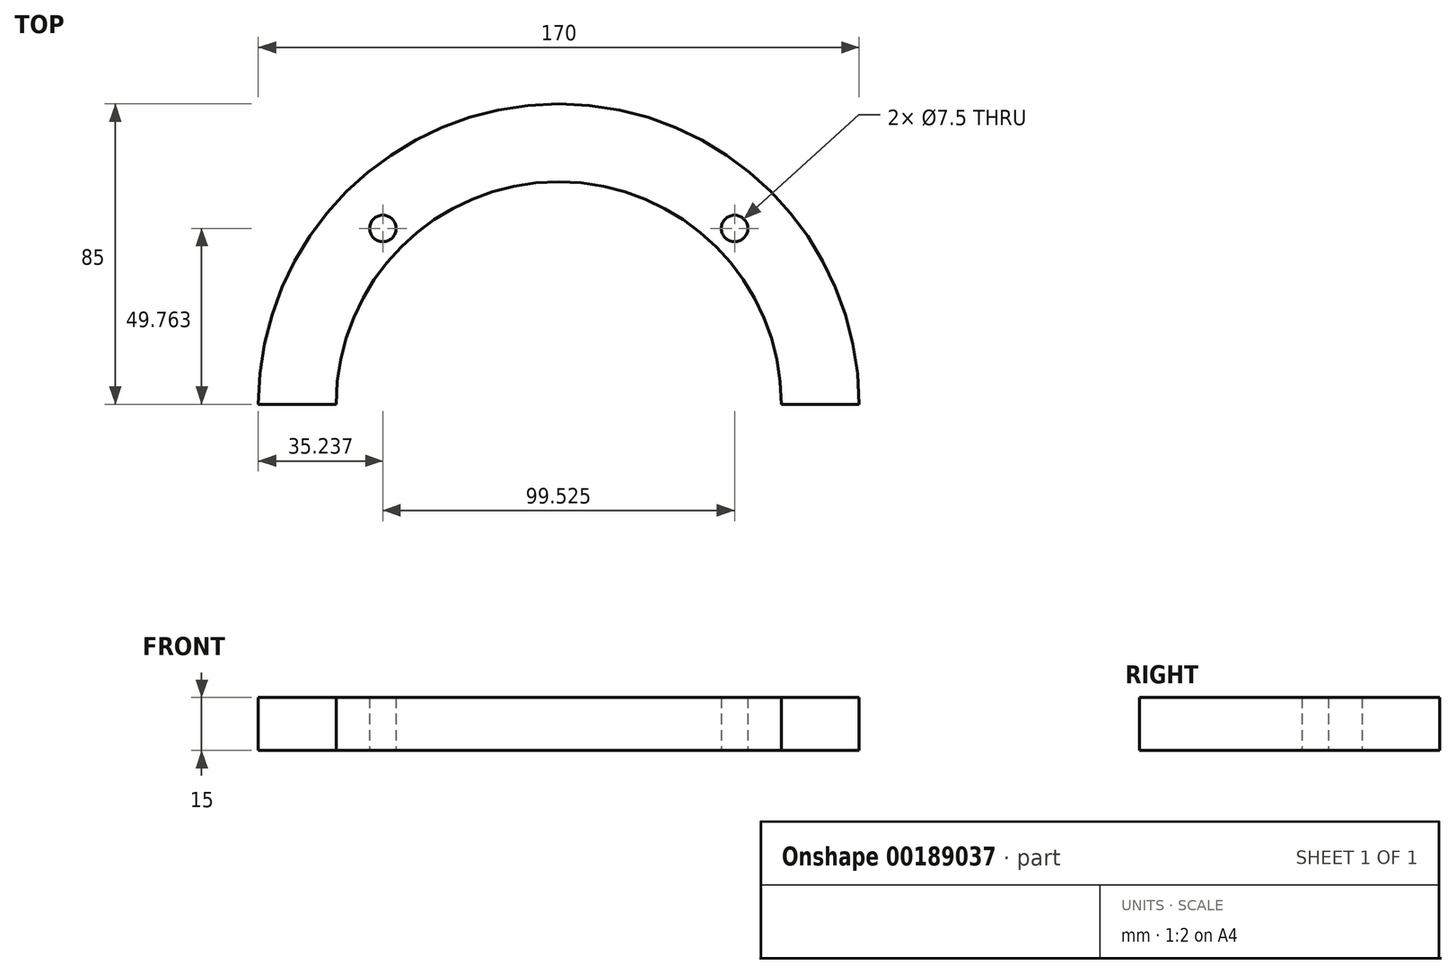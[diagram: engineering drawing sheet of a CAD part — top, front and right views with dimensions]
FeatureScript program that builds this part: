
annotation { "Feature Type Name" : "Feature", "Feature Type Description" : "" }
export const myFeature = defineFeature(function(context is Context, id is Id, definition is map)
    precondition{}
    {
        {
            var Q0;
            Q0=qCreatedBy(makeId("Top.planeOp"),FACE);
            var sketch = newSketch(context, id + "F0", { "sketchPlane" : qUnion([Q0])});
            skArc(sketch, "E0", {"start": v(85, 0) * mm, "mid": v(0, 85) * mm, "end": v(-85, 0) * mm});
            skArc(sketch, "E1", {"start": v(70.38, 0) * mm, "mid": v(0, 70.38) * mm, "end": v(-70.38, 0) * mm, "construction": true});
            skArc(sketch, "E2", {"start": v(63, 0) * mm, "mid": v(0, 63) * mm, "end": v(-63, 0) * mm});
            skLineSegment(sketch, "E3", {"start": v(0, 0) * mm, "end": v(-49.76, 49.76) * mm, "construction": true});
            skLineSegment(sketch, "E4", {"start": v(0, 0) * mm, "end": v(-70.38, 0) * mm, "construction": true});
            skCircle(sketch, "E5", {"center": v(-49.76, 49.76) * mm, "radius": 3.75 * mm});
            skLineSegment(sketch, "E6.2.0", {"start": v(0, 0) * mm, "end": v(70.38, 0) * mm, "construction": true});
            skLineSegment(sketch, "E7.2.3.0", {"start": v(0, 63) * mm, "end": v(0, 70.38) * mm, "construction": true});
            skCircle(sketch, "E7.3.3.0", {"center": v(49.76, 49.76) * mm, "radius": 3.75 * mm});
            skLineSegment(sketch, "E8", {"start": v(-85, 0) * mm, "end": v(-63, 0) * mm});
            skLineSegment(sketch, "E9", {"start": v(63, 0) * mm, "end": v(85, 0) * mm});
            skSolve(sketch);
        }
        {
            var Q0;
            Q0 = qSketchRegion(id + "F0", true);
            extrude(context, id + "F1", {"entities" : qUnion([Q0]), "depth" : 15 * mm});
        }
    });
